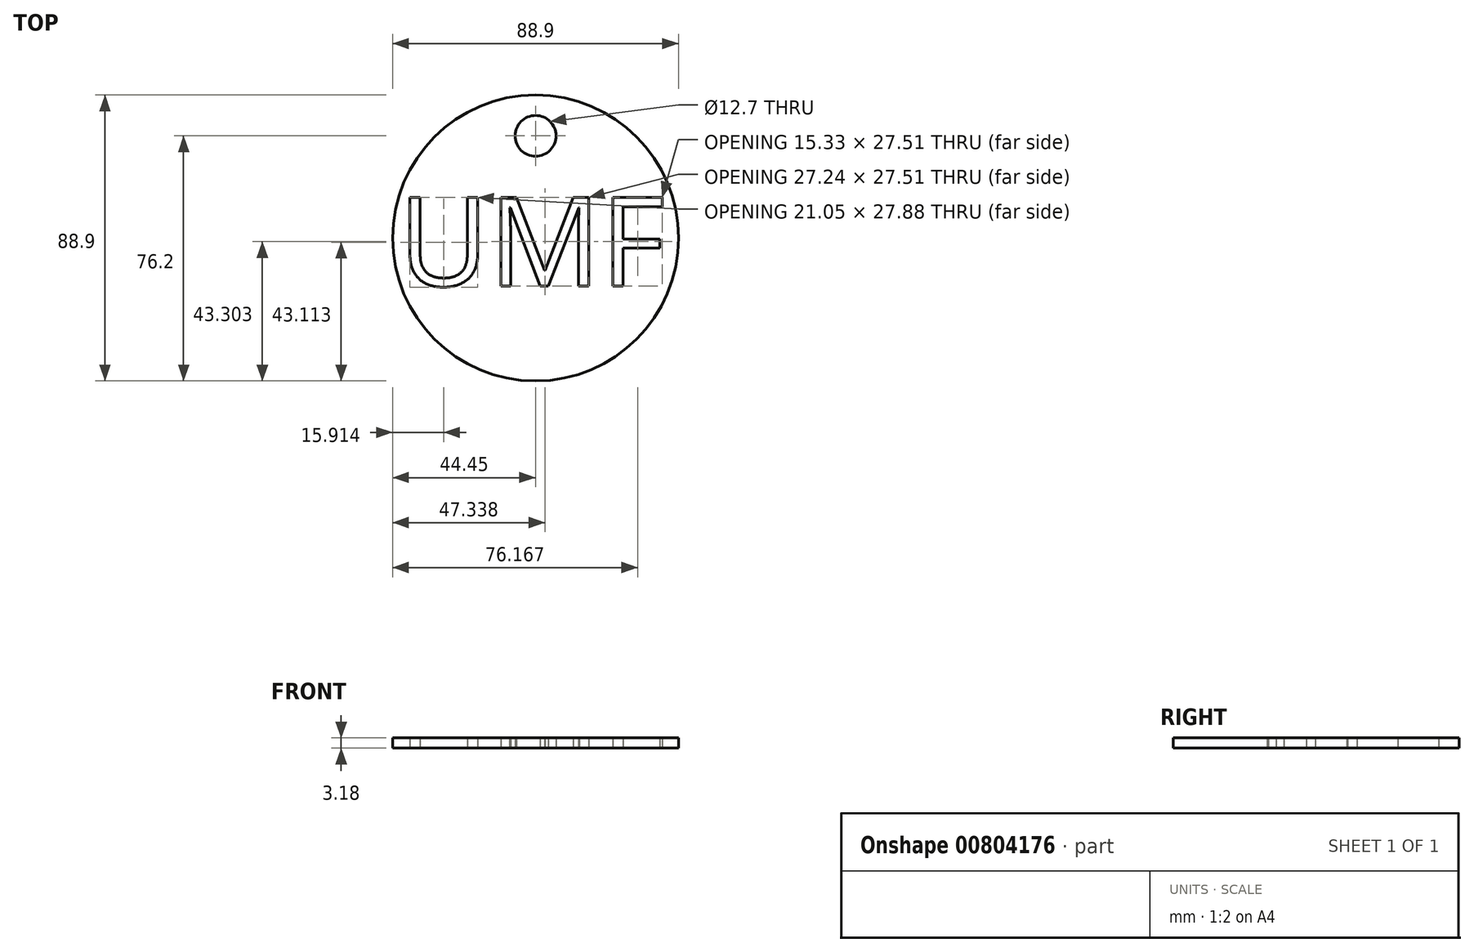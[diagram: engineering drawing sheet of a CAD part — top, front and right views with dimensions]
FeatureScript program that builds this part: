
annotation { "Feature Type Name" : "Feature", "Feature Type Description" : "" }
export const myFeature = defineFeature(function(context is Context, id is Id, definition is map)
    precondition{}
    {
        {
            var Q0;
            Q0=qCreatedBy(makeId("Top.planeOp"),FACE);
            var sketch = newSketch(context, id + "F0", { "sketchPlane" : qUnion([Q0])});
            skCircle(sketch, "E0", {"center": v(0, 0) * mm, "radius": 44.45 * mm});
            skCircle(sketch, "E1", {"center": v(0, 31.75) * mm, "radius": 6.35 * mm});
            skText(sketch, "E2", { "text": "UMF", "fontName": "OpenSans-Regular.ttf"});
            const initialGuessF0  = {"E2": [-0.04256, -0.0149, 1, 0, 0.02774]};
            skSetInitialGuess(sketch, initialGuessF0);
            skSolve(sketch);
        }
        {
            var Q0;
            Q0=makeQuery(id+"F0.imprint","IMPRINT",FACE,{"disambiguationData":[TD([[makeQuery(id+"F0.imprint","IMPRINT",EDGE,{"derivedFrom":sQuery(id+"F0.wireOp",EDGE,"E0")}),1.0]])]});
            extrude(context, id + "F1", {"entities" : qUnion([Q0]), "depth" : 3.17 * mm, "offsetDistance" : 25.4 * mm});
        }
    });
